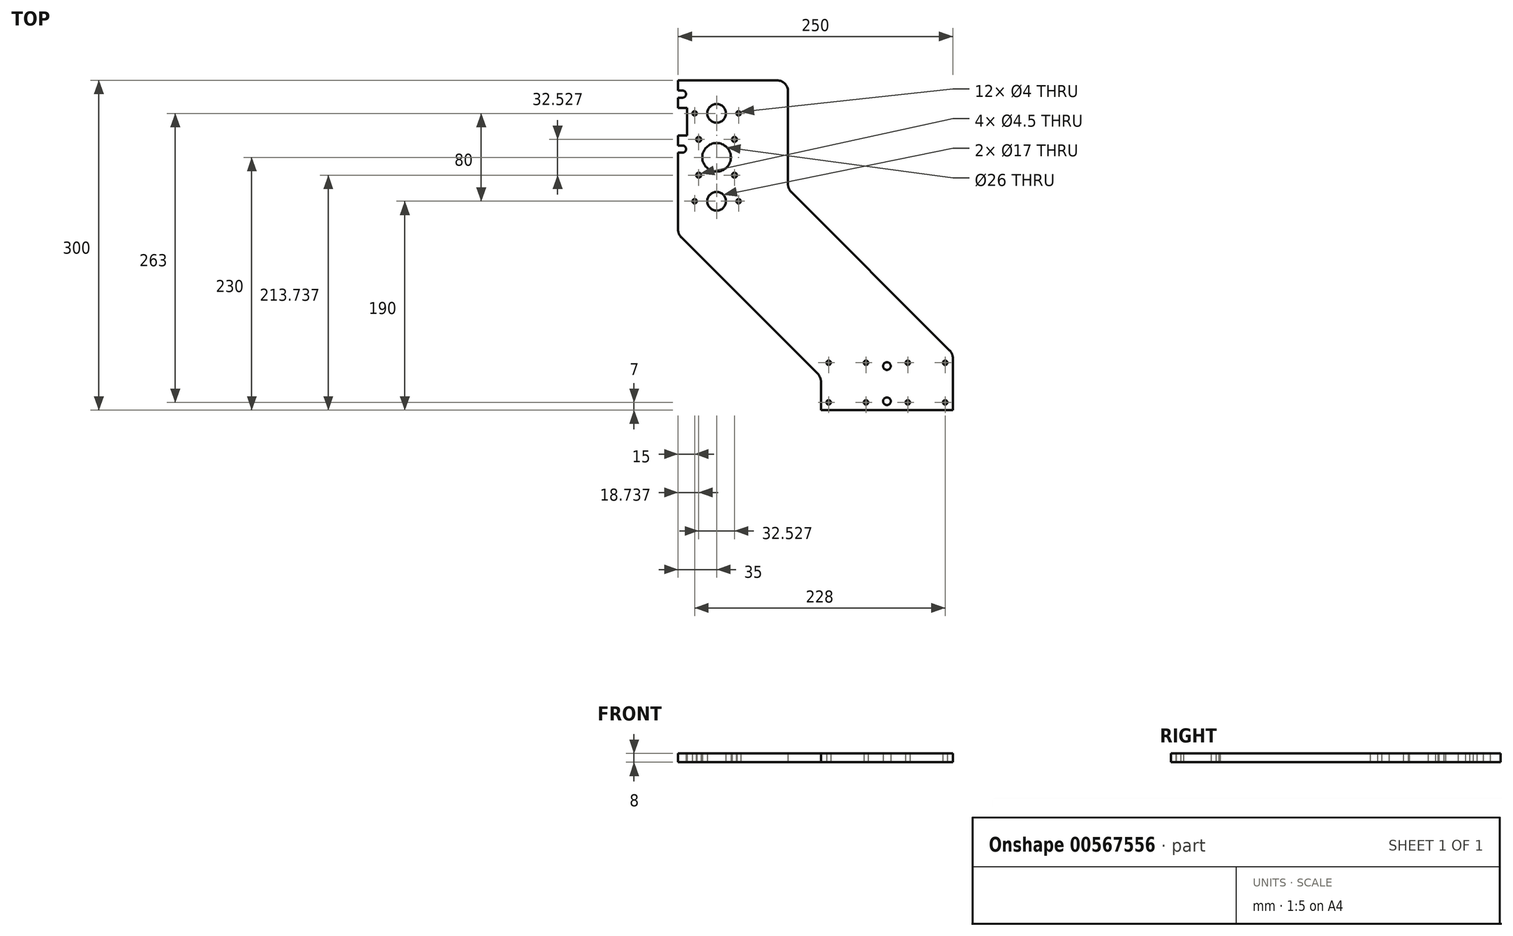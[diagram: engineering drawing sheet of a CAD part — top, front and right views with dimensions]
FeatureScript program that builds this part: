
annotation { "Feature Type Name" : "Feature", "Feature Type Description" : "" }
export const myFeature = defineFeature(function(context is Context, id is Id, definition is map)
    precondition{}
    {
        {
            var Q0;
            Q0=qCreatedBy(makeId("Top.planeOp"),FACE);
            var sketch = newSketch(context, id + "F0", { "sketchPlane" : qUnion([Q0])});
            skLineSegment(sketch, "E0", {"start": v(0, 0) * mm, "end": v(120, 0) * mm});
            skLineSegment(sketch, "E1", {"start": v(120, 0) * mm, "end": v(120, 51.42) * mm});
            skLineSegment(sketch, "E2", {"start": v(120, 51.42) * mm, "end": v(-30, 201.42) * mm});
            skLineSegment(sketch, "E3", {"start": v(-30, 201.42) * mm, "end": v(-30, 300) * mm});
            skLineSegment(sketch, "E4", {"start": v(-30, 300) * mm, "end": v(-130, 300) * mm});
            skLineSegment(sketch, "E5", {"start": v(-130, 300) * mm, "end": v(-130, 290.75) * mm});
            skLineSegment(sketch, "E6", {"start": v(-130, 160) * mm, "end": v(0, 30) * mm});
            skLineSegment(sketch, "E7", {"start": v(0, 30) * mm, "end": v(0, 0) * mm});
            skCircle(sketch, "E8", {"center": v(7, 43) * mm, "radius": 2 * mm});
            skCircle(sketch, "E9", {"center": v(7, 7) * mm, "radius": 2 * mm});
            skCircle(sketch, "E10", {"center": v(41, 43) * mm, "radius": 2 * mm});
            skCircle(sketch, "E11", {"center": v(41, 7) * mm, "radius": 2 * mm});
            skLineSegment(sketch, "E12", {"start": v(60, 0) * mm, "end": v(60, 107.18) * mm, "construction": true});
            skCircle(sketch, "E13.MirrorC", {"center": v(79, 43) * mm, "radius": 2 * mm});
            skCircle(sketch, "E14.MirrorC", {"center": v(113, 43) * mm, "radius": 2 * mm});
            skCircle(sketch, "E15.MirrorC", {"center": v(113, 7) * mm, "radius": 2 * mm});
            skCircle(sketch, "E16.MirrorC", {"center": v(79, 7) * mm, "radius": 2 * mm});
            skCircle(sketch, "E17", {"center": v(-95, 270) * mm, "radius": 8.5 * mm});
            skCircle(sketch, "E18", {"center": v(-95, 190) * mm, "radius": 8.5 * mm});
            skPoint(sketch, "E19", {"position": v(-80, 300) * mm});
            skCircle(sketch, "E20", {"center": v(-75, 270) * mm, "radius": 2 * mm});
            skCircle(sketch, "E21", {"center": v(-115, 270) * mm, "radius": 2 * mm});
            skCircle(sketch, "E22", {"center": v(-75, 190) * mm, "radius": 2 * mm});
            skCircle(sketch, "E23", {"center": v(-115, 190) * mm, "radius": 2 * mm});
            skLineSegment(sketch, "E24", {"start": v(-115, 190) * mm, "end": v(-75, 190) * mm, "construction": true});
            skLineSegment(sketch, "E25", {"start": v(-75, 270) * mm, "end": v(-115, 270) * mm, "construction": true});
            skLineSegment(sketch, "E26.bottom", {"start": v(-130, 275) * mm, "end": v(-122, 275) * mm});
            skLineSegment(sketch, "E26.top", {"start": v(-130, 250) * mm, "end": v(-122, 250) * mm});
            skLineSegment(sketch, "E26.right", {"start": v(-122, 275) * mm, "end": v(-122, 250) * mm});
            skLineSegment(sketch, "E27.trimOffspring", {"start": v(-130, 250) * mm, "end": v(-130, 160) * mm});
            skArc(sketch, "E28", {"start": v(-126, 284.25) * mm, "mid": v(-122.75, 287.5) * mm, "end": v(-126, 290.75) * mm});
            skLineSegment(sketch, "E29", {"start": v(-126, 290.75) * mm, "end": v(-130, 290.75) * mm});
            skLineSegment(sketch, "E30", {"start": v(-126, 284.25) * mm, "end": v(-130, 284.25) * mm});
            skLineSegment(sketch, "E31.trimOffspring", {"start": v(-130, 284.25) * mm, "end": v(-130, 275) * mm});
            skLineSegment(sketch, "E32", {"start": v(-89.75, 262.5) * mm, "end": v(-122, 262.5) * mm, "construction": true});
            skLineSegment(sketch, "E33.MirrorCS", {"start": v(-126, 240.75) * mm, "end": v(-130, 240.75) * mm});
            skArc(sketch, "E34.MirrorCS", {"start": v(-126, 240.75) * mm, "mid": v(-122.75, 237.5) * mm, "end": v(-126, 234.25) * mm});
            skLineSegment(sketch, "E35.MirrorCS", {"start": v(-126, 234.25) * mm, "end": v(-130, 234.25) * mm});
            skCircle(sketch, "E36", {"center": v(60, 8) * mm, "radius": 3.5 * mm});
            skCircle(sketch, "E37", {"center": v(60, 40) * mm, "radius": 3.5 * mm});
            skCircle(sketch, "E38", {"center": v(-95, 230) * mm, "radius": 23 * mm, "construction": true});
            skLineSegment(sketch, "E39.bottom", {"start": v(-78.74, 213.74) * mm, "end": v(-111.26, 213.74) * mm, "construction": true});
            skLineSegment(sketch, "E39.top", {"start": v(-78.74, 246.26) * mm, "end": v(-111.26, 246.26) * mm, "construction": true});
            skLineSegment(sketch, "E39.left", {"start": v(-78.74, 213.74) * mm, "end": v(-78.74, 246.26) * mm, "construction": true});
            skLineSegment(sketch, "E39.right", {"start": v(-111.26, 213.74) * mm, "end": v(-111.26, 246.26) * mm, "construction": true});
            skCircle(sketch, "E40", {"center": v(-78.74, 213.74) * mm, "radius": 2.25 * mm});
            skCircle(sketch, "E41", {"center": v(-111.26, 213.74) * mm, "radius": 2.25 * mm});
            skCircle(sketch, "E42", {"center": v(-111.26, 246.26) * mm, "radius": 2.25 * mm});
            skCircle(sketch, "E43", {"center": v(-78.74, 246.26) * mm, "radius": 2.25 * mm});
            skCircle(sketch, "E44", {"center": v(-95, 230) * mm, "radius": 13 * mm});
            skSolve(sketch);
        }
        {
            var Q0;
            Q0=makeQuery(id+"F0.imprint","IMPRINT",FACE,{"disambiguationData":[TD([[makeQuery(id+"F0.imprint","IMPRINT",EDGE,{"derivedFrom":sQuery(id+"F0.wireOp",EDGE,"E0")}),1.0]])]});
            extrude(context, id + "F1", {"entities" : qUnion([Q0]), "depth" : 8 * mm, "offsetDistance" : 25 * mm});
        }
        {
            var Q0;
            Q0=makeQuery(id+"F1.opExtrude","SWEPT_EDGE",EDGE,{"disambiguationData":[OSD([sQuery(id+"F0.wireOp",EDGE,"E3"),sQuery(id+"F0.wireOp",EDGE,"E4")])]});
            var Q1;
            Q1=makeQuery(id+"F1.opExtrude","SWEPT_EDGE",EDGE,{"disambiguationData":[OSD([sQuery(id+"F0.wireOp",EDGE,"E2"),sQuery(id+"F0.wireOp",EDGE,"E3")])]});
            var Q2;
            Q2=makeQuery(id+"F1.opExtrude","SWEPT_EDGE",EDGE,{"disambiguationData":[OSD([sQuery(id+"F0.wireOp",EDGE,"E6"),sQuery(id+"F0.wireOp",EDGE,"E27.trimOffspring")])]});
            var Q3;
            Q3=makeQuery(id+"F1.opExtrude","SWEPT_EDGE",EDGE,{"disambiguationData":[OSD([sQuery(id+"F0.wireOp",EDGE,"E6"),sQuery(id+"F0.wireOp",EDGE,"E7")])]});
            var Q4;
            Q4=makeQuery(id+"F1.opExtrude","SWEPT_EDGE",EDGE,{"disambiguationData":[OSD([sQuery(id+"F0.wireOp",EDGE,"E1"),sQuery(id+"F0.wireOp",EDGE,"E2")])]});
            fillet(context, id + "F2", {"entities" : qUnion([Q0, Q1, Q2, Q3, Q4]), "radius" : 10 * mm, "tangentPropagation" : true, "allowEdgeOverflow" : false});
        }
    });
